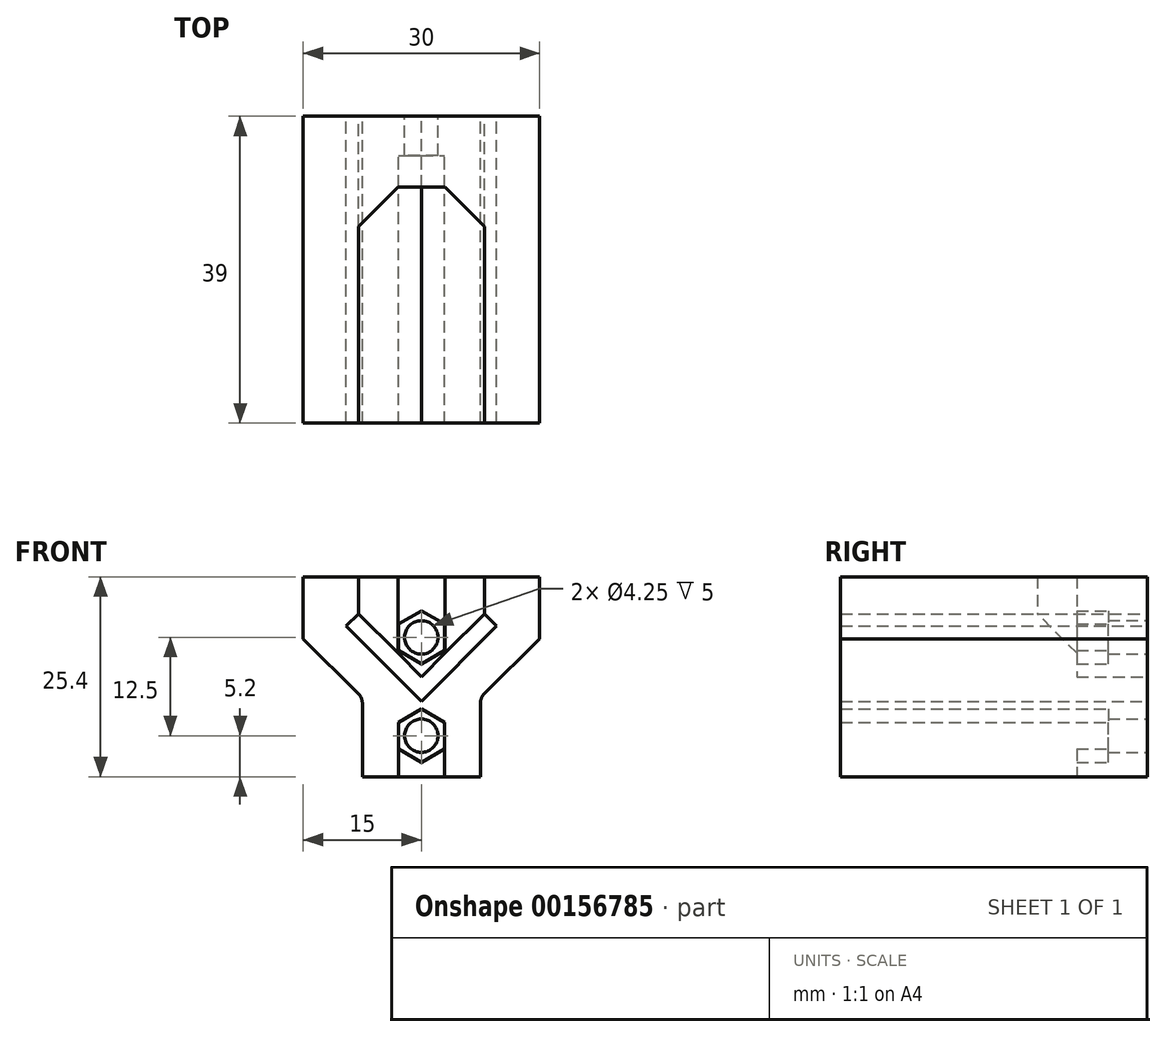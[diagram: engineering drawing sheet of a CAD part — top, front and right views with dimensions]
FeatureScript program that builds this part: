
annotation { "Feature Type Name" : "Feature", "Feature Type Description" : "" }
export const myFeature = defineFeature(function(context is Context, id is Id, definition is map)
    precondition{}
    {
        {
            var Q0;
            Q0=qCreatedBy(makeId("Front.planeOp"),FACE);
            var sketch = newSketch(context, id + "F0", { "sketchPlane" : qUnion([Q0])});
            skLineSegment(sketch, "E0.bottom", {"start": v(7.5, -12.7) * mm, "end": v(-7.5, -12.7) * mm});
            skLineSegment(sketch, "E0.top", {"start": v(15, 12.7) * mm, "end": v(-15, 12.7) * mm});
            skLineSegment(sketch, "E0.left", {"start": v(15, 4.82) * mm, "end": v(15, 12.7) * mm});
            skLineSegment(sketch, "E0.right", {"start": v(-15, 4.82) * mm, "end": v(-15, 12.7) * mm});
            skPoint(sketch, "E0.middle", {"position": v(0, 0) * mm});
            skCircle(sketch, "E1", {"center": v(0, 5) * mm, "radius": 2.12 * mm});
            skCircle(sketch, "E2", {"center": v(0, -7.5) * mm, "radius": 2.12 * mm});
            skLineSegment(sketch, "E3", {"start": v(-8, 8) * mm, "end": v(0, 0) * mm});
            skLineSegment(sketch, "E4", {"start": v(0, 0) * mm, "end": v(8, 8) * mm});
            skLineSegment(sketch, "E5", {"start": v(8, 8) * mm, "end": v(9.55, 6.43) * mm});
            skLineSegment(sketch, "E6", {"start": v(9.55, 6.43) * mm, "end": v(0, -3.11) * mm});
            skLineSegment(sketch, "E7", {"start": v(0, -3.11) * mm, "end": v(-9.55, 6.43) * mm});
            skLineSegment(sketch, "E8", {"start": v(-9.55, 6.43) * mm, "end": v(-8, 8) * mm});
            skLineSegment(sketch, "E9", {"start": v(-15, 4.82) * mm, "end": v(-7.5, -2.68) * mm});
            skLineSegment(sketch, "E10", {"start": v(-7.5, -2.68) * mm, "end": v(-7.5, -12.7) * mm});
            skLineSegment(sketch, "E11.MirrorCS", {"start": v(15, 4.82) * mm, "end": v(7.5, -2.68) * mm});
            skLineSegment(sketch, "E12.MirrorCS", {"start": v(7.5, -2.68) * mm, "end": v(7.5, -12.7) * mm});
            skPoint(sketch, "E13.orphan", {"position": v(-15, -12.7) * mm});
            skPoint(sketch, "E14.orphan", {"position": v(15, -12.7) * mm});
            skSolve(sketch);
        }
        {
            var Q0;
            Q0 = qSketchRegion(id + "F0", true);
            extrude(context, id + "F1", {"entities" : qUnion([Q0]), "depth" : 5 * mm});
        }
        {
            var Q0;
            Q0=makeQuery(id+"F1.opExtrude","CAP_FACE",FACE,{"disambiguationData":[OSD([sQuery(id+"F0.wireOp",EDGE,"E0.bottom"),sQuery(id+"F0.wireOp",EDGE,"E0.top"),sQuery(id+"F0.wireOp",EDGE,"E0.left"),sQuery(id+"F0.wireOp",EDGE,"E0.right"),sQuery(id+"F0.wireOp",EDGE,"E1"),sQuery(id+"F0.wireOp",EDGE,"E2"),sQuery(id+"F0.wireOp",EDGE,"E3"),sQuery(id+"F0.wireOp",EDGE,"E4"),sQuery(id+"F0.wireOp",EDGE,"E5"),sQuery(id+"F0.wireOp",EDGE,"E6"),sQuery(id+"F0.wireOp",EDGE,"E7"),sQuery(id+"F0.wireOp",EDGE,"E8")])],"isStart":false});
            var sketch = newSketch(context, id + "F2", { "sketchPlane" : qUnion([Q0])});
            skCircle(sketch, "E15.cCircle", {"center": v(0, 5) * mm, "radius": 2.93 * mm, "construction": true});
            skLineSegment(sketch, "E15.0", {"start": v(2.93, 6.69) * mm, "end": v(2.93, 3.31) * mm});
            skLineSegment(sketch, "E15.1", {"start": v(2.93, 3.31) * mm, "end": v(0, 1.62) * mm});
            skLineSegment(sketch, "E15.2", {"start": v(0, 1.62) * mm, "end": v(-2.93, 3.31) * mm});
            skLineSegment(sketch, "E15.3", {"start": v(-2.92, 3.31) * mm, "end": v(-2.92, 6.69) * mm});
            skLineSegment(sketch, "E15.4", {"start": v(-2.93, 6.69) * mm, "end": v(0, 8.38) * mm});
            skLineSegment(sketch, "E15.5", {"start": v(0, 8.38) * mm, "end": v(2.93, 6.69) * mm});
            skPoint(sketch, "E15.0.midPoint", {"position": v(2.93, 5) * mm});
            skCircle(sketch, "E16.cCircle", {"center": v(0, -7.5) * mm, "radius": 2.93 * mm, "construction": true});
            skLineSegment(sketch, "E16.0", {"start": v(2.93, -5.81) * mm, "end": v(2.93, -9.19) * mm});
            skLineSegment(sketch, "E16.1", {"start": v(2.93, -9.19) * mm, "end": v(0, -10.88) * mm});
            skLineSegment(sketch, "E16.2", {"start": v(0, -10.88) * mm, "end": v(-2.93, -9.19) * mm});
            skLineSegment(sketch, "E16.3", {"start": v(-2.93, -9.19) * mm, "end": v(-2.93, -5.81) * mm});
            skLineSegment(sketch, "E16.4", {"start": v(-2.92, -5.81) * mm, "end": v(0, -4.12) * mm});
            skLineSegment(sketch, "E16.5", {"start": v(0, -4.12) * mm, "end": v(2.93, -5.81) * mm});
            skPoint(sketch, "E16.0.midPoint", {"position": v(2.93, -7.5) * mm});
            skLineSegment(sketch, "E17", {"start": v(-8, 8) * mm, "end": v(0, 0) * mm});
            skLineSegment(sketch, "E18", {"start": v(0, 0) * mm, "end": v(8, 8) * mm});
            skLineSegment(sketch, "E19", {"start": v(8, 12.7) * mm, "end": v(-8, 12.7) * mm});
            skLineSegment(sketch, "E20", {"start": v(0, -12.7) * mm, "end": v(7.5, -12.7) * mm});
            skLineSegment(sketch, "E21", {"start": v(7.5, -12.7) * mm, "end": v(7.5, -2.68) * mm});
            skLineSegment(sketch, "E22", {"start": v(7.5, -2.68) * mm, "end": v(7.5, -2.68) * mm});
            skLineSegment(sketch, "E23", {"start": v(9.55, 6.43) * mm, "end": v(0, -3.11) * mm});
            skLineSegment(sketch, "E24", {"start": v(0, -3.11) * mm, "end": v(-9.55, 6.43) * mm});
            skLineSegment(sketch, "E25", {"start": v(-7.5, -2.68) * mm, "end": v(-7.5, -2.68) * mm});
            skLineSegment(sketch, "E26", {"start": v(-7.5, -2.68) * mm, "end": v(-7.5, -12.7) * mm});
            skLineSegment(sketch, "E27", {"start": v(-7.5, -12.7) * mm, "end": v(0, -12.7) * mm});
            skLineSegment(sketch, "E28", {"start": v(-7.5, -2.68) * mm, "end": v(-15, 4.82) * mm});
            skLineSegment(sketch, "E29", {"start": v(-15, 4.82) * mm, "end": v(-15, 12.7) * mm});
            skLineSegment(sketch, "E30", {"start": v(-15, 12.7) * mm, "end": v(-8, 12.7) * mm});
            skLineSegment(sketch, "E31", {"start": v(-8, 8) * mm, "end": v(-9.55, 6.43) * mm});
            skLineSegment(sketch, "E32", {"start": v(8, 8) * mm, "end": v(9.55, 6.43) * mm});
            skLineSegment(sketch, "E33", {"start": v(8, 12.7) * mm, "end": v(15, 12.7) * mm});
            skLineSegment(sketch, "E34", {"start": v(15, 12.7) * mm, "end": v(15, 4.82) * mm});
            skLineSegment(sketch, "E35", {"start": v(15, 4.82) * mm, "end": v(7.5, -2.68) * mm});
            skSolve(sketch);
        }
        {
            var Q0;
            Q0 = qSketchRegion(id + "F2", true);
            extrude(context, id + "F3", {"entities" : qUnion([Q0]), "operationType" : NewBodyOperationType.ADD, "depth" : 4 * mm});
        }
        {
            var Q0;
            Q0=makeQuery(id+"F3.opExtrude","CAP_FACE",FACE,{"disambiguationData":[OSD([sQuery(id+"F2.wireOp",EDGE,"E15.0"),sQuery(id+"F2.wireOp",EDGE,"E15.1"),sQuery(id+"F2.wireOp",EDGE,"E15.2"),sQuery(id+"F2.wireOp",EDGE,"E15.3"),sQuery(id+"F2.wireOp",EDGE,"E15.4"),sQuery(id+"F2.wireOp",EDGE,"E15.5"),sQuery(id+"F2.wireOp",EDGE,"E16.0"),sQuery(id+"F2.wireOp",EDGE,"E16.1"),sQuery(id+"F2.wireOp",EDGE,"E16.2"),sQuery(id+"F2.wireOp",EDGE,"E16.3"),sQuery(id+"F2.wireOp",EDGE,"E16.4"),sQuery(id+"F2.wireOp",EDGE,"E16.5"),sQuery(id+"F2.wireOp",EDGE,"E17"),sQuery(id+"F2.wireOp",EDGE,"E18"),sQuery(id+"F2.wireOp",EDGE,"E19"),sQuery(id+"F2.wireOp",EDGE,"E20"),sQuery(id+"F2.wireOp",EDGE,"E21"),sQuery(id+"F2.wireOp",EDGE,"E23"),sQuery(id+"F2.wireOp",EDGE,"E24"),sQuery(id+"F2.wireOp",EDGE,"E26"),sQuery(id+"F2.wireOp",EDGE,"E27"),sQuery(id+"F2.wireOp",EDGE,"E28"),sQuery(id+"F2.wireOp",EDGE,"E29"),sQuery(id+"F2.wireOp",EDGE,"E30"),sQuery(id+"F2.wireOp",EDGE,"E31"),sQuery(id+"F2.wireOp",EDGE,"E32"),sQuery(id+"F2.wireOp",EDGE,"E33"),sQuery(id+"F2.wireOp",EDGE,"E34"),sQuery(id+"F2.wireOp",EDGE,"E35")])],"isStart":false});
            var sketch = newSketch(context, id + "F4", { "sketchPlane" : qUnion([Q0])});
            skLineSegment(sketch, "E36", {"start": v(-15, 12.7) * mm, "end": v(-15, 4.82) * mm});
            skLineSegment(sketch, "E37", {"start": v(-15, 4.82) * mm, "end": v(-7.5, -2.68) * mm});
            skLineSegment(sketch, "E38", {"start": v(-7.5, -2.68) * mm, "end": v(-7.5, -5.81) * mm});
            skLineSegment(sketch, "E39", {"start": v(-2.92, -5.81) * mm, "end": v(0, -4.12) * mm});
            skLineSegment(sketch, "E40", {"start": v(0, -4.12) * mm, "end": v(2.93, -5.81) * mm});
            skLineSegment(sketch, "E41", {"start": v(7.5, -5.81) * mm, "end": v(7.5, -2.68) * mm});
            skLineSegment(sketch, "E42", {"start": v(7.5, -2.68) * mm, "end": v(15, 4.82) * mm});
            skLineSegment(sketch, "E43.MirrorCS", {"start": v(15, 12.7) * mm, "end": v(15, 4.82) * mm});
            skLineSegment(sketch, "E44", {"start": v(8, 8) * mm, "end": v(9.55, 6.43) * mm});
            skLineSegment(sketch, "E45", {"start": v(9.55, 6.43) * mm, "end": v(0, -3.11) * mm});
            skLineSegment(sketch, "E46", {"start": v(0, -3.11) * mm, "end": v(-9.55, 6.43) * mm});
            skLineSegment(sketch, "E47", {"start": v(-9.55, 6.43) * mm, "end": v(-8, 8) * mm});
            skLineSegment(sketch, "E48", {"start": v(-7.5, -5.81) * mm, "end": v(-7.5, -12.7) * mm});
            skLineSegment(sketch, "E49", {"start": v(-7.5, -12.7) * mm, "end": v(-2.92, -12.7) * mm});
            skLineSegment(sketch, "E50", {"start": v(-2.92, -12.7) * mm, "end": v(-2.92, -5.81) * mm});
            skLineSegment(sketch, "E51.MirrorCS", {"start": v(7.5, -5.81) * mm, "end": v(7.5, -12.7) * mm});
            skLineSegment(sketch, "E52.MirrorCS", {"start": v(2.92, -12.7) * mm, "end": v(2.92, -5.81) * mm});
            skLineSegment(sketch, "E53.MirrorCS", {"start": v(7.5, -12.7) * mm, "end": v(2.92, -12.7) * mm});
            skLineSegment(sketch, "E54", {"start": v(-15, 12.7) * mm, "end": v(-8, 12.7) * mm});
            skLineSegment(sketch, "E55", {"start": v(-8, 8) * mm, "end": v(-8, 12.7) * mm});
            skLineSegment(sketch, "E56.MirrorCS", {"start": v(15, 12.7) * mm, "end": v(8, 12.7) * mm});
            skLineSegment(sketch, "E57.MirrorCS", {"start": v(8, 8) * mm, "end": v(8, 12.7) * mm});
            skSolve(sketch);
        }
        {
            var Q0;
            Q0 = qSketchRegion(id + "F4", true);
            extrude(context, id + "F5", {"entities" : qUnion([Q0]), "operationType" : NewBodyOperationType.ADD, "depth" : 30 * mm});
        }
        {
            var Q0;
            Q0=makeQuery(id+"F5.boolean.opBoolean","MERGE",FACE,{"derivedFrom":[makeQuery(id+"F3.boolean.opBoolean","MERGE",FACE,{"derivedFrom":[makeQuery(id+"F1.opExtrude","SWEPT_FACE",FACE,{"disambiguationData":[OSD([sQuery(id+"F0.wireOp",EDGE,"E7")])]}),makeQuery(id+"F3.opExtrude","SWEPT_FACE",FACE,{"disambiguationData":[OSD([sQuery(id+"F2.wireOp",EDGE,"E24")])]})]}),makeQuery(id+"F5.opExtrude","SWEPT_FACE",FACE,{"disambiguationData":[OSD([sQuery(id+"F4.wireOp",EDGE,"E46")])]})]});
            var sketch = newSketch(context, id + "F6", { "sketchPlane" : qUnion([Q0])});
            skCircle(sketch, "E58", {"center": v(-6.3, -31.5) * mm, "radius": 2.12 * mm});
            skCircle(sketch, "E59", {"center": v(-6.3, -16.5) * mm, "radius": 2.12 * mm});
            skSolve(sketch);
        }
        {
            var Q0;
            Q0 = qSketchRegion(id + "F6", true);
            extrude(context, id + "F7", {"entities" : qUnion([Q0]), "operationType" : NewBodyOperationType.REMOVE, "oppositeDirection" : true, "depth" : 25 * mm});
        }
        {
            var Q0;
            Q0=makeQuery(id+"F5.boolean.opBoolean","MERGE",FACE,{"derivedFrom":[makeQuery(id+"F3.boolean.opBoolean","MERGE",FACE,{"derivedFrom":[makeQuery(id+"F1.opExtrude","SWEPT_FACE",FACE,{"disambiguationData":[OSD([sQuery(id+"F0.wireOp",EDGE,"E9")])]}),makeQuery(id+"F3.opExtrude","SWEPT_FACE",FACE,{"disambiguationData":[OSD([sQuery(id+"F2.wireOp",EDGE,"E28")])]})]}),makeQuery(id+"F5.opExtrude","SWEPT_FACE",FACE,{"disambiguationData":[OSD([sQuery(id+"F4.wireOp",EDGE,"E37")])]})]});
            var sketch = newSketch(context, id + "F8", { "sketchPlane" : qUnion([Q0])});
            skCircle(sketch, "E60.cCircle", {"center": v(-6.3, 16.5) * mm, "radius": 2.93 * mm, "construction": true});
            skLineSegment(sketch, "E60.0", {"start": v(-9.22, 14.81) * mm, "end": v(-9.22, 18.19) * mm});
            skLineSegment(sketch, "E60.1", {"start": v(-9.22, 18.19) * mm, "end": v(-6.3, 19.88) * mm});
            skLineSegment(sketch, "E60.2", {"start": v(-6.3, 19.88) * mm, "end": v(-3.37, 18.19) * mm});
            skLineSegment(sketch, "E60.3", {"start": v(-3.37, 18.19) * mm, "end": v(-3.37, 14.81) * mm});
            skLineSegment(sketch, "E60.4", {"start": v(-3.37, 14.81) * mm, "end": v(-6.3, 13.12) * mm});
            skLineSegment(sketch, "E60.5", {"start": v(-6.3, 13.12) * mm, "end": v(-9.23, 14.81) * mm});
            skPoint(sketch, "E60.0.midPoint", {"position": v(-9.22, 16.5) * mm});
            skCircle(sketch, "E61.cCircle", {"center": v(-6.3, 31.5) * mm, "radius": 2.93 * mm, "construction": true});
            skLineSegment(sketch, "E61.0", {"start": v(-9.22, 29.81) * mm, "end": v(-9.22, 33.19) * mm});
            skLineSegment(sketch, "E61.1", {"start": v(-9.22, 33.19) * mm, "end": v(-6.3, 34.88) * mm});
            skLineSegment(sketch, "E61.2", {"start": v(-6.3, 34.88) * mm, "end": v(-3.37, 33.19) * mm});
            skLineSegment(sketch, "E61.3", {"start": v(-3.37, 33.19) * mm, "end": v(-3.37, 29.81) * mm});
            skLineSegment(sketch, "E61.4", {"start": v(-3.37, 29.81) * mm, "end": v(-6.3, 28.12) * mm});
            skLineSegment(sketch, "E61.5", {"start": v(-6.3, 28.12) * mm, "end": v(-9.22, 29.81) * mm});
            skPoint(sketch, "E61.0.midPoint", {"position": v(-9.22, 31.5) * mm});
            skSolve(sketch);
        }
        {
            var Q0;
            Q0 = qSketchRegion(id + "F8", true);
            extrude(context, id + "F9", {"entities" : qUnion([Q0]), "operationType" : NewBodyOperationType.REMOVE, "oppositeDirection" : true, "depth" : 3 * mm});
        }
        {
            var Q0;
            {var subQ0=sQuery(id+"F0.wireOp",EDGE,"E10");var subQ1=sQuery(id+"F2.wireOp",EDGE,"E26");var subQ2=sQuery(id+"F4.wireOp",EDGE,"E38");Q0=makeQuery(id+"F9.boolean.opBoolean","SPLIT",EDGE,{"disambiguationData":[topologyDisambiguationEdgeConnected([makeQuery(id+"F1.opExtrude","SWEPT_FACE",FACE,{"disambiguationData":[OSD([subQ0])]}),makeQuery(id+"F3.opExtrude","SWEPT_FACE",FACE,{"disambiguationData":[OSD([subQ1])]}),makeQuery(id+"F5.opExtrude","SWEPT_FACE",FACE,{"disambiguationData":[OSD([subQ2,sQuery(id+"F4.wireOp",EDGE,"E48")])]}),makeQuery(id+"F9.opExtrude","CAP_FACE",FACE,{"disambiguationData":[OSD([sQuery(id+"F8.wireOp",EDGE,"E60.0"),sQuery(id+"F8.wireOp",EDGE,"E60.1"),sQuery(id+"F8.wireOp",EDGE,"E60.2"),sQuery(id+"F8.wireOp",EDGE,"E60.3"),sQuery(id+"F8.wireOp",EDGE,"E60.4"),sQuery(id+"F8.wireOp",EDGE,"E60.5")])],"isStart":true})])],"derivedFrom":makeQuery(id+"F5.boolean.opBoolean","MERGE",EDGE,{"derivedFrom":[makeQuery(id+"F3.boolean.opBoolean","MERGE",EDGE,{"derivedFrom":[makeQuery(id+"F1.opExtrude","SWEPT_EDGE",EDGE,{"disambiguationData":[OSD([sQuery(id+"F0.wireOp",EDGE,"E9"),subQ0])]}),makeQuery(id+"F3.opExtrude","SWEPT_EDGE",EDGE,{"disambiguationData":[OSD([subQ1,sQuery(id+"F2.wireOp",EDGE,"E28")])]})]}),makeQuery(id+"F5.opExtrude","SWEPT_EDGE",EDGE,{"disambiguationData":[OSD([sQuery(id+"F4.wireOp",EDGE,"E37"),subQ2])]})]})});}
            var Q1;
            {var subQ0=sQuery(id+"F0.wireOp",EDGE,"E10");var subQ1=sQuery(id+"F2.wireOp",EDGE,"E26");var subQ2=sQuery(id+"F4.wireOp",EDGE,"E38");Q1=makeQuery(id+"F9.boolean.opBoolean","SPLIT",EDGE,{"disambiguationData":[topologyDisambiguationEdgeConnected([makeQuery(id+"F1.opExtrude","SWEPT_FACE",FACE,{"disambiguationData":[OSD([subQ0])]}),makeQuery(id+"F3.opExtrude","SWEPT_FACE",FACE,{"disambiguationData":[OSD([subQ1])]}),makeQuery(id+"F5.opExtrude","SWEPT_FACE",FACE,{"disambiguationData":[OSD([subQ2,sQuery(id+"F4.wireOp",EDGE,"E48")])]}),makeQuery(id+"F9.opExtrude","CAP_FACE",FACE,{"disambiguationData":[OSD([sQuery(id+"F8.wireOp",EDGE,"E61.0"),sQuery(id+"F8.wireOp",EDGE,"E61.1"),sQuery(id+"F8.wireOp",EDGE,"E61.2"),sQuery(id+"F8.wireOp",EDGE,"E61.3"),sQuery(id+"F8.wireOp",EDGE,"E61.4"),sQuery(id+"F8.wireOp",EDGE,"E61.5")])],"isStart":true})])],"derivedFrom":makeQuery(id+"F5.boolean.opBoolean","MERGE",EDGE,{"derivedFrom":[makeQuery(id+"F3.boolean.opBoolean","MERGE",EDGE,{"derivedFrom":[makeQuery(id+"F1.opExtrude","SWEPT_EDGE",EDGE,{"disambiguationData":[OSD([sQuery(id+"F0.wireOp",EDGE,"E9"),subQ0])]}),makeQuery(id+"F3.opExtrude","SWEPT_EDGE",EDGE,{"disambiguationData":[OSD([subQ1,sQuery(id+"F2.wireOp",EDGE,"E28")])]})]}),makeQuery(id+"F5.opExtrude","SWEPT_EDGE",EDGE,{"disambiguationData":[OSD([sQuery(id+"F4.wireOp",EDGE,"E37"),subQ2])]})]})});}
            var Q2;
            {var subQ0=sQuery(id+"F0.wireOp",EDGE,"E12.MirrorCS");var subQ1=sQuery(id+"F2.wireOp",EDGE,"E21");var subQ2=sQuery(id+"F4.wireOp",EDGE,"E41");Q2=makeQuery(id+"F4LVu3fbzSdGnBf_1.1.F9.boolean.opBoolean","SPLIT",EDGE,{"disambiguationData":[topologyDisambiguationEdgeConnected([makeQuery(id+"F1.opExtrude","SWEPT_FACE",FACE,{"disambiguationData":[OSD([subQ0])]}),makeQuery(id+"F3.opExtrude","SWEPT_FACE",FACE,{"disambiguationData":[OSD([subQ1])]}),makeQuery(id+"F5.opExtrude","SWEPT_FACE",FACE,{"disambiguationData":[OSD([subQ2,sQuery(id+"F4.wireOp",EDGE,"E51.MirrorCS")])]}),makeQuery(id+"F4LVu3fbzSdGnBf_1.1.F9.opExtrude","CAP_FACE",FACE,{"disambiguationData":[OSD([sQuery(id+"F8.wireOp",EDGE,"E61.0"),sQuery(id+"F8.wireOp",EDGE,"E61.1"),sQuery(id+"F8.wireOp",EDGE,"E61.2"),sQuery(id+"F8.wireOp",EDGE,"E61.3"),sQuery(id+"F8.wireOp",EDGE,"E61.4"),sQuery(id+"F8.wireOp",EDGE,"E61.5")])],"isStart":true})])],"derivedFrom":makeQuery(id+"F5.boolean.opBoolean","MERGE",EDGE,{"derivedFrom":[makeQuery(id+"F3.boolean.opBoolean","MERGE",EDGE,{"derivedFrom":[makeQuery(id+"F1.opExtrude","SWEPT_EDGE",EDGE,{"disambiguationData":[OSD([sQuery(id+"F0.wireOp",EDGE,"E11.MirrorCS"),subQ0])]}),makeQuery(id+"F3.opExtrude","SWEPT_EDGE",EDGE,{"disambiguationData":[OSD([subQ1,sQuery(id+"F2.wireOp",EDGE,"E35")])]})]}),makeQuery(id+"F5.opExtrude","SWEPT_EDGE",EDGE,{"disambiguationData":[OSD([subQ2,sQuery(id+"F4.wireOp",EDGE,"E42")])]})]})});}
            var Q3;
            {var subQ0=sQuery(id+"F0.wireOp",EDGE,"E12.MirrorCS");var subQ1=sQuery(id+"F2.wireOp",EDGE,"E21");var subQ2=sQuery(id+"F4.wireOp",EDGE,"E41");Q3=makeQuery(id+"F4LVu3fbzSdGnBf_1.1.F9.boolean.opBoolean","SPLIT",EDGE,{"disambiguationData":[topologyDisambiguationEdgeConnected([makeQuery(id+"F1.opExtrude","SWEPT_FACE",FACE,{"disambiguationData":[OSD([subQ0])]}),makeQuery(id+"F3.opExtrude","SWEPT_FACE",FACE,{"disambiguationData":[OSD([subQ1])]}),makeQuery(id+"F5.opExtrude","SWEPT_FACE",FACE,{"disambiguationData":[OSD([subQ2,sQuery(id+"F4.wireOp",EDGE,"E51.MirrorCS")])]}),makeQuery(id+"F4LVu3fbzSdGnBf_1.1.F9.opExtrude","CAP_FACE",FACE,{"disambiguationData":[OSD([sQuery(id+"F8.wireOp",EDGE,"E60.0"),sQuery(id+"F8.wireOp",EDGE,"E60.1"),sQuery(id+"F8.wireOp",EDGE,"E60.2"),sQuery(id+"F8.wireOp",EDGE,"E60.3"),sQuery(id+"F8.wireOp",EDGE,"E60.4"),sQuery(id+"F8.wireOp",EDGE,"E60.5")])],"isStart":true})])],"derivedFrom":makeQuery(id+"F5.boolean.opBoolean","MERGE",EDGE,{"derivedFrom":[makeQuery(id+"F3.boolean.opBoolean","MERGE",EDGE,{"derivedFrom":[makeQuery(id+"F1.opExtrude","SWEPT_EDGE",EDGE,{"disambiguationData":[OSD([sQuery(id+"F0.wireOp",EDGE,"E11.MirrorCS"),subQ0])]}),makeQuery(id+"F3.opExtrude","SWEPT_EDGE",EDGE,{"disambiguationData":[OSD([subQ1,sQuery(id+"F2.wireOp",EDGE,"E35")])]})]}),makeQuery(id+"F5.opExtrude","SWEPT_EDGE",EDGE,{"disambiguationData":[OSD([subQ2,sQuery(id+"F4.wireOp",EDGE,"E42")])]})]})});}
            fillet(context, id + "F10", {"entities" : qUnion([Q0, Q1, Q2, Q3]), "radius" : 1.6 * mm, "tangentPropagation" : true, "allowEdgeOverflow" : false});
        }
        {
            var Q0;
            Q0=makeQuery(id+"F5.opExtrude","CAP_EDGE",EDGE,{"disambiguationData":[OSD([sQuery(id+"F4.wireOp",EDGE,"E55")])],"isStart":true});
            var Q1;
            Q1=makeQuery(id+"F5.opExtrude","CAP_EDGE",EDGE,{"disambiguationData":[OSD([sQuery(id+"F4.wireOp",EDGE,"E57.MirrorCS")])],"isStart":true});
            chamfer(context, id + "F11", {"entities" : qUnion([Q0, Q1]), "width" : 5 * mm, "tangentPropagation" : true});
        }
    });
